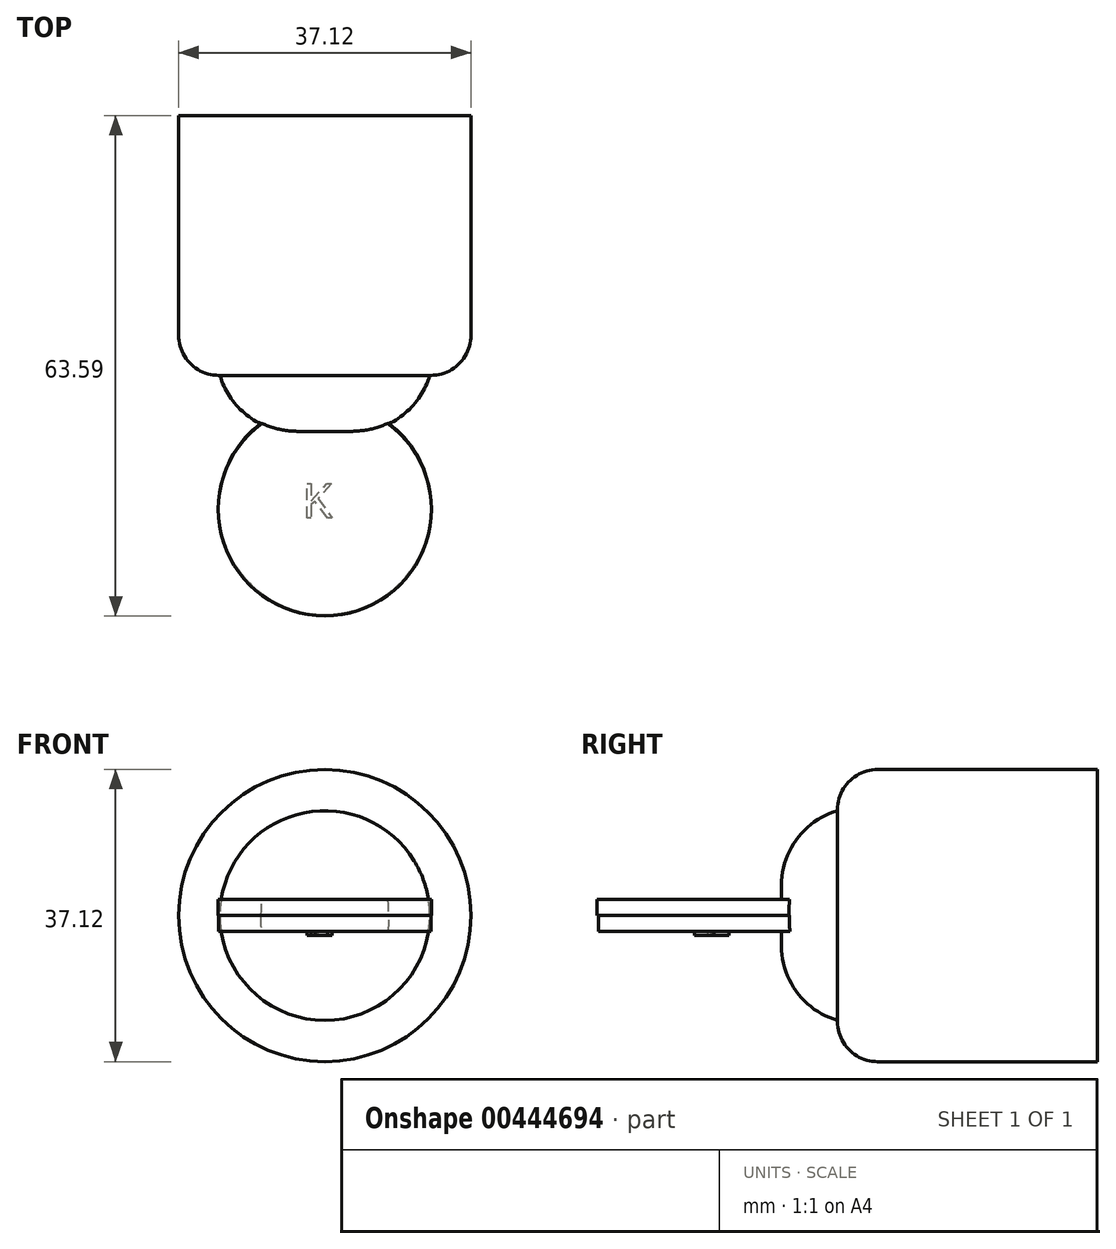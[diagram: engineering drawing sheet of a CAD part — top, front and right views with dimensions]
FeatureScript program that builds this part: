
annotation { "Feature Type Name" : "Feature", "Feature Type Description" : "" }
export const myFeature = defineFeature(function(context is Context, id is Id, definition is map)
    precondition{}
    {
        {
            var Q0;
            Q0=qCreatedBy(makeId("Front.planeOp"),FACE);
            var sketch = newSketch(context, id + "F0", { "sketchPlane" : qUnion([Q0])});
            skCircle(sketch, "E0", {"center": v(0, 0) * mm, "radius": 18.56 * mm});
            skSolve(sketch);
        }
        {
            var Q0;
            Q0 = qSketchRegion(id + "F0", true);
            extrude(context, id + "F1", {"entities" : qUnion([Q0]), "depth" : 33.02 * mm});
        }
        {
            var Q0;
            Q0=makeQuery(id+"F1.opExtrude","CAP_FACE",FACE,{"disambiguationData":[OSD([sQuery(id+"F0.wireOp",EDGE,"E0")])],"isStart":false});
            fillet(context, id + "F2", {"entities" : qUnion([Q0]), "radius" : 5.08 * mm, "tangentPropagation" : true, "allowEdgeOverflow" : false});
        }
        {
            var Q0;
            Q0=qCreatedBy(makeId("Front.planeOp"),FACE);
            var sketch = newSketch(context, id + "F3", { "sketchPlane" : qUnion([Q0])});
            skCircle(sketch, "E1", {"center": v(0, 0) * mm, "radius": 13.32 * mm});
            skSolve(sketch);
        }
        {
            var Q0;
            Q0 = qSketchRegion(id + "F3", true);
            extrude(context, id + "F4", {"entities" : qUnion([Q0]), "operationType" : NewBodyOperationType.ADD, "depth" : 40.13 * mm});
        }
        {
            var Q0;
            Q0=makeQuery(id+"F4.opExtrude","CAP_EDGE",EDGE,{"disambiguationData":[OSD([sQuery(id+"F3.wireOp",EDGE,"E1")])],"isStart":false});
            fillet(context, id + "F5", {"entities" : qUnion([Q0]), "radius" : 9.8 * mm, "tangentPropagation" : true, "allowEdgeOverflow" : false});
        }
        {
            var Q0;
            Q0=qCreatedBy(makeId("Top.planeOp"),FACE);
            var sketch = newSketch(context, id + "F6", { "sketchPlane" : qUnion([Q0])});
            skCircle(sketch, "E2", {"center": v(0, -49.9) * mm, "radius": 13.5 * mm});
            skSolve(sketch);
        }
        {
            var Q0;
            Q0=makeQuery(id+"F6.imprint","IMPRINT",FACE,{"disambiguationData":[TD([[makeQuery(id+"F6.imprint","IMPRINT",EDGE,{"derivedFrom":sQuery(id+"F6.wireOp",EDGE,"E2")}),1.0]])]});
            extrude(context, id + "F7", {"entities" : qUnion([Q0]), "operationType" : NewBodyOperationType.ADD, "oppositeDirection" : true, "depth" : 2.03 * mm});
        }
        {
            var Q0;
            Q0=qCreatedBy(makeId("Top.planeOp"),FACE);
            var sketch = newSketch(context, id + "F8", { "sketchPlane" : qUnion([Q0])});
            skCircle(sketch, "E3", {"center": v(0, -50.06) * mm, "radius": 13.53 * mm});
            skSolve(sketch);
        }
        {
            var Q0;
            Q0 = qSketchRegion(id + "F8", true);
            extrude(context, id + "F9", {"entities" : qUnion([Q0]), "operationType" : NewBodyOperationType.ADD, "depth" : 2.03 * mm});
        }
        {
            var Q0;
            Q0=qCreatedBy(makeId("Top.planeOp"),FACE);
            var sketch = newSketch(context, id + "F10", { "sketchPlane" : qUnion([Q0])});
            skText(sketch, "E4", { "text": "K", "fontName": "OpenSans-Regular.ttf"});
            const initialGuessF10  = {"E4": [-0.00283, -0.05117, 1, 0, 0.00442]};
            skSetInitialGuess(sketch, initialGuessF10);
            skSolve(sketch);
        }
        {
            var Q0;
            Q0 = qSketchRegion(id + "F10", true);
            extrude(context, id + "F11", {"entities" : qUnion([Q0]), "operationType" : NewBodyOperationType.ADD, "oppositeDirection" : true, "depth" : 2.54 * mm});
        }
    });
